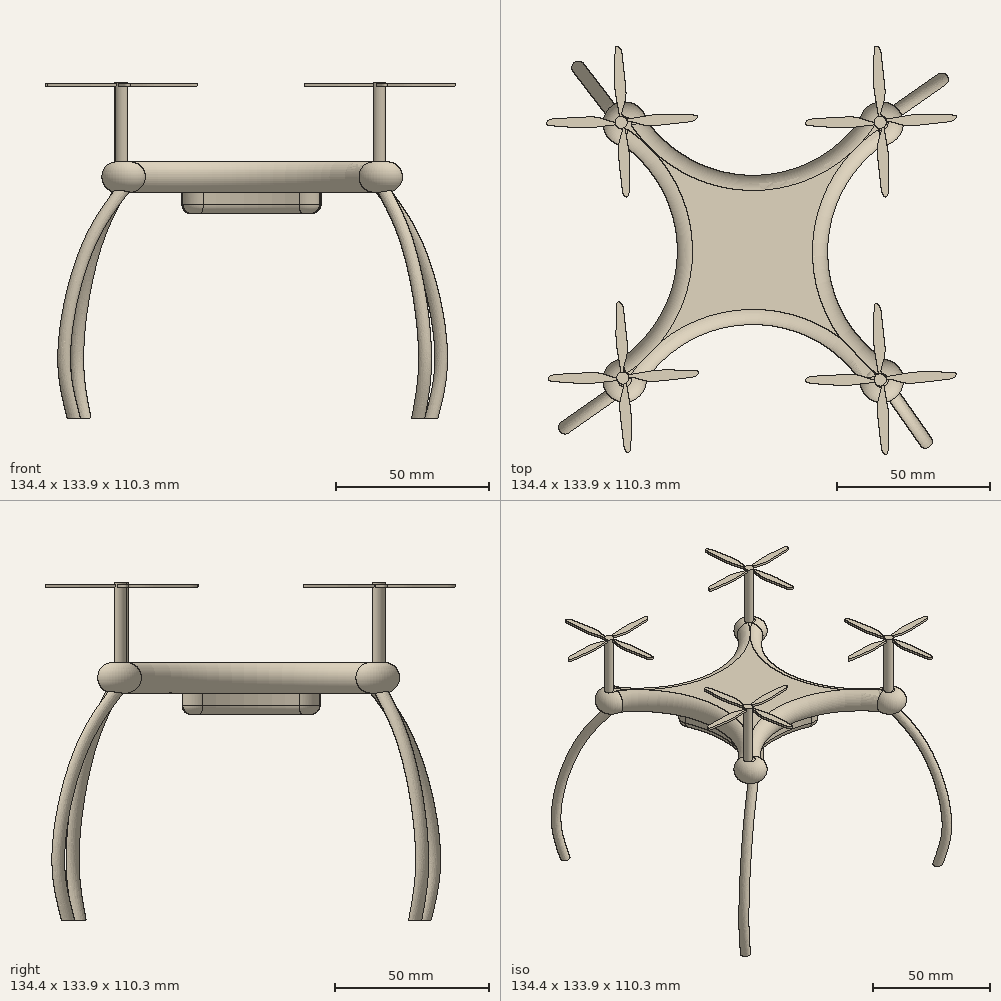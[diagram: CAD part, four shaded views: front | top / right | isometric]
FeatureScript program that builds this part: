
annotation { "Feature Type Name" : "Feature", "Feature Type Description" : "" }
export const myFeature = defineFeature(function(context is Context, id is Id, definition is map)
    precondition{}
    {
        {
            var Q0;
            Q0=qCreatedBy(makeId("Top.planeOp"),FACE);
            var sketch = newSketch(context, id + "F0", { "sketchPlane" : qUnion([Q0])});
            skLineSegment(sketch, "E0.bottom", {"start": v(0, 0) * mm, "end": v(-100, 0) * mm, "construction": true});
            skLineSegment(sketch, "E0.top", {"start": v(0, -100) * mm, "end": v(-100, -100) * mm, "construction": true});
            skLineSegment(sketch, "E0.left", {"start": v(0, 0) * mm, "end": v(0, -100) * mm, "construction": true});
            skLineSegment(sketch, "E0.right", {"start": v(-100, 0) * mm, "end": v(-100, -100) * mm, "construction": true});
            skLineSegment(sketch, "E1", {"start": v(-100, -100) * mm, "end": v(0, 0) * mm, "construction": true});
            skLineSegment(sketch, "E2", {"start": v(-100, 0) * mm, "end": v(0, -100) * mm, "construction": true});
            skArc(sketch, "E3", {"start": v(-93.38, -85.34) * mm, "mid": v(-96.6, -97.94) * mm, "end": v(-85, -92.07) * mm});
            skArc(sketch, "E4", {"start": v(-15, -92.07) * mm, "mid": v(-50, -74.05) * mm, "end": v(-85, -92.07) * mm});
            skArc(sketch, "E5", {"start": v(-15, -92.07) * mm, "mid": v(-3.07, -97.77) * mm, "end": v(-7.58, -85.34) * mm});
            skArc(sketch, "E6", {"start": v(-7.58, -15.34) * mm, "mid": v(-25.6, -50.34) * mm, "end": v(-7.58, -85.34) * mm});
            skArc(sketch, "E7", {"start": v(-7.58, -15.34) * mm, "mid": v(-2.64, -3.44) * mm, "end": v(-15, -7.1) * mm});
            skArc(sketch, "E8", {"start": v(-85, -7.1) * mm, "mid": v(-50, -25.12) * mm, "end": v(-15, -7.1) * mm});
            skArc(sketch, "E9", {"start": v(-85, -7.1) * mm, "mid": v(-97.36, -3.44) * mm, "end": v(-92.43, -15.34) * mm});
            skArc(sketch, "E10", {"start": v(-93.38, -85.34) * mm, "mid": v(-74.89, -50.59) * mm, "end": v(-92.43, -15.34) * mm});
            skSolve(sketch);
        }
        {
            var Q0;
            Q0=makeQuery(id+"F0.imprint","IMPRINT",FACE,{"disambiguationData":[TD([[makeQuery(id+"F0.imprint","IMPRINT",EDGE,{"derivedFrom":sQuery(id+"F0.wireOp",EDGE,"E3")}),1.0]])]});
            extrude(context, id + "F1", {"entities" : qUnion([Q0]), "depth" : 10 * mm, "offsetDistance" : 25 * mm});
        }
        {
            var Q0;
            Q0=makeQuery(id+"F1.opExtrude","CAP_FACE",FACE,{"disambiguationData":[OSD([sQuery(id+"F0.wireOp",EDGE,"E3"),sQuery(id+"F0.wireOp",EDGE,"E4"),sQuery(id+"F0.wireOp",EDGE,"E5"),sQuery(id+"F0.wireOp",EDGE,"E6"),sQuery(id+"F0.wireOp",EDGE,"E7"),sQuery(id+"F0.wireOp",EDGE,"E8"),sQuery(id+"F0.wireOp",EDGE,"E9"),sQuery(id+"F0.wireOp",EDGE,"E10")])],"isStart":false});
            var Q1;
            Q1=makeQuery(id+"F1.opExtrude","CAP_FACE",FACE,{"disambiguationData":[OSD([sQuery(id+"F0.wireOp",EDGE,"E3"),sQuery(id+"F0.wireOp",EDGE,"E4"),sQuery(id+"F0.wireOp",EDGE,"E5"),sQuery(id+"F0.wireOp",EDGE,"E6"),sQuery(id+"F0.wireOp",EDGE,"E7"),sQuery(id+"F0.wireOp",EDGE,"E8"),sQuery(id+"F0.wireOp",EDGE,"E9"),sQuery(id+"F0.wireOp",EDGE,"E10")])],"isStart":true});
            fillet(context, id + "F2", {"entities" : qUnion([Q0, Q1]), "radius" : 5 * mm, "tangentPropagation" : true, "allowEdgeOverflow" : false});
        }
        {
            var Q0;
            Q0=qCreatedBy(makeId("Right.planeOp"),FACE);
            var sketch = newSketch(context, id + "F3", { "sketchPlane" : qUnion([Q0])});
            skFitSpline(sketch, "E11", {"points": [v(21, 0.3) * mm, v(17.73, 12.66) * mm, v(17.36, 24.3) * mm, v(19.55, 37.01) * mm, v(23.54, 49.37) * mm, v(33, 66.1) * mm, v(46.08, 79.9) * mm, v(46.8, 80.27) * mm], "startDerivative": vector(-26.02, 82.97) * mm, "endDerivative": vector(13.83, 3.74) * mm});
            skSolve(sketch);
        }
        {
            var Q0;
            Q0=qCreatedBy(makeId("Top.planeOp"),FACE);
            var sketch = newSketch(context, id + "F4", { "sketchPlane" : qUnion([Q0])});
            skCircle(sketch, "E12", {"center": v(0.33, 21.02) * mm, "radius": 2.16 * mm});
            skSolve(sketch);
        }
        {
            var Q0;
            Q0=makeQuery(id+"F4.imprint","IMPRINT",FACE,{"disambiguationData":[TD([[makeQuery(id+"F4.imprint","IMPRINT",EDGE,{"derivedFrom":sQuery(id+"F4.wireOp",EDGE,"E12")}),1.0]])]});
            var Q1;
            Q1=sQuery(id+"F3.wireOp",EDGE,"E11");
            sweep(context, id + "F5", {"profiles" : qUnion([Q0]), "path" : qUnion([Q1])});
        }
        {
            var Q0;
            Q0=makeQuery(id+"F5.opSweep","SWEPT_BODY",BODY,{"disambiguationData":[OSD([sQuery(id+"F3.wireOp",EDGE,"E11"),sQuery(id+"F4.wireOp",EDGE,"E12")])]});
            transform(context, id + "F6", {"entities" : qUnion([Q0]), "transformType" : TransformType.TRANSLATION_3D, "dx" : -7.8 * mm, "dy" : -134.3 * mm, "dz" : -74.2 * mm, "makeCopy" : false});
        }
        {
            var Q0;
            Q0=makeQuery(id+"F2.opFillet","SPLIT",FACE,{"disambiguationData":[OD(4.0)],"derivedFrom":makeQuery(id+"F1.opExtrude","CAP_FACE",FACE,{"disambiguationData":[OSD([sQuery(id+"F0.wireOp",EDGE,"E3"),sQuery(id+"F0.wireOp",EDGE,"E4"),sQuery(id+"F0.wireOp",EDGE,"E5"),sQuery(id+"F0.wireOp",EDGE,"E6"),sQuery(id+"F0.wireOp",EDGE,"E7"),sQuery(id+"F0.wireOp",EDGE,"E8"),sQuery(id+"F0.wireOp",EDGE,"E9"),sQuery(id+"F0.wireOp",EDGE,"E10")])],"isStart":true})});
            extrude(context, id + "F7", {"entities" : qUnion([Q0]), "operationType" : NewBodyOperationType.ADD, "depth" : 7 * mm, "offsetDistance" : 25 * mm});
        }
        {
            var Q0;
            {var subQ0=sQuery(id+"F0.wireOp",EDGE,"E10");var subQ1=sQuery(id+"F0.wireOp",EDGE,"E9");var subQ2=sQuery(id+"F0.wireOp",EDGE,"E8");var subQ3=sQuery(id+"F0.wireOp",EDGE,"E7");var subQ4=sQuery(id+"F0.wireOp",EDGE,"E6");var subQ5=sQuery(id+"F0.wireOp",EDGE,"E5");var subQ6=sQuery(id+"F0.wireOp",EDGE,"E4");var subQ7=sQuery(id+"F0.wireOp",EDGE,"E3");Q0=makeQuery(id+"F7.opExtrude","SWEPT_EDGE",EDGE,{"disambiguationData":[OSD([subQ7,subQ6,subQ5,subQ4,subQ3,subQ2,subQ1,subQ0]),TDD([makeQuery(id+"F2.opFillet","BLEND_VERTEX",VERTEX,{"disambiguationData":[OD(1.0)],"blendedFrom":[makeQuery(id+"F1.opExtrude","CAP_EDGE",EDGE,{"disambiguationData":[OSD([subQ4])],"isStart":true}),makeQuery(id+"F1.opExtrude","CAP_EDGE",EDGE,{"disambiguationData":[OSD([subQ2])],"isStart":true}),makeQuery(id+"F1.opExtrude","CAP_FACE",FACE,{"disambiguationData":[OSD([subQ7,subQ6,subQ5,subQ4,subQ3,subQ2,subQ1,subQ0])],"isStart":true})],"blendedInto":[makeQuery(id+"F1.opExtrude","CAP_FACE",FACE,{"disambiguationData":[OSD([subQ7,subQ6,subQ5,subQ4,subQ3,subQ2,subQ1,subQ0])],"isStart":true})]})])]});}
            var Q1;
            {var subQ0=sQuery(id+"F0.wireOp",EDGE,"E10");var subQ1=sQuery(id+"F0.wireOp",EDGE,"E9");var subQ2=sQuery(id+"F0.wireOp",EDGE,"E8");var subQ3=sQuery(id+"F0.wireOp",EDGE,"E7");var subQ4=sQuery(id+"F0.wireOp",EDGE,"E6");var subQ5=sQuery(id+"F0.wireOp",EDGE,"E5");var subQ6=sQuery(id+"F0.wireOp",EDGE,"E4");var subQ7=sQuery(id+"F0.wireOp",EDGE,"E3");Q1=makeQuery(id+"F7.opExtrude","SWEPT_EDGE",EDGE,{"disambiguationData":[OSD([subQ7,subQ6,subQ5,subQ4,subQ3,subQ2,subQ1,subQ0]),TDD([makeQuery(id+"F2.opFillet","BLEND_VERTEX",VERTEX,{"disambiguationData":[OD(1.0)],"blendedFrom":[makeQuery(id+"F1.opExtrude","CAP_EDGE",EDGE,{"disambiguationData":[OSD([subQ6])],"isStart":true}),makeQuery(id+"F1.opExtrude","CAP_EDGE",EDGE,{"disambiguationData":[OSD([subQ4])],"isStart":true}),makeQuery(id+"F1.opExtrude","CAP_FACE",FACE,{"disambiguationData":[OSD([subQ7,subQ6,subQ5,subQ4,subQ3,subQ2,subQ1,subQ0])],"isStart":true})],"blendedInto":[makeQuery(id+"F1.opExtrude","CAP_FACE",FACE,{"disambiguationData":[OSD([subQ7,subQ6,subQ5,subQ4,subQ3,subQ2,subQ1,subQ0])],"isStart":true})]})])]});}
            var Q2;
            {var subQ0=sQuery(id+"F0.wireOp",EDGE,"E10");var subQ1=sQuery(id+"F0.wireOp",EDGE,"E9");var subQ2=sQuery(id+"F0.wireOp",EDGE,"E8");var subQ3=sQuery(id+"F0.wireOp",EDGE,"E7");var subQ4=sQuery(id+"F0.wireOp",EDGE,"E6");var subQ5=sQuery(id+"F0.wireOp",EDGE,"E5");var subQ6=sQuery(id+"F0.wireOp",EDGE,"E4");var subQ7=sQuery(id+"F0.wireOp",EDGE,"E3");Q2=makeQuery(id+"F7.opExtrude","SWEPT_EDGE",EDGE,{"disambiguationData":[OSD([subQ7,subQ6,subQ5,subQ4,subQ3,subQ2,subQ1,subQ0]),TDD([makeQuery(id+"F2.opFillet","BLEND_VERTEX",VERTEX,{"disambiguationData":[OD(1.0)],"blendedFrom":[makeQuery(id+"F1.opExtrude","CAP_EDGE",EDGE,{"disambiguationData":[OSD([subQ6])],"isStart":true}),makeQuery(id+"F1.opExtrude","CAP_EDGE",EDGE,{"disambiguationData":[OSD([subQ0])],"isStart":true}),makeQuery(id+"F1.opExtrude","CAP_FACE",FACE,{"disambiguationData":[OSD([subQ7,subQ6,subQ5,subQ4,subQ3,subQ2,subQ1,subQ0])],"isStart":true})],"blendedInto":[makeQuery(id+"F1.opExtrude","CAP_FACE",FACE,{"disambiguationData":[OSD([subQ7,subQ6,subQ5,subQ4,subQ3,subQ2,subQ1,subQ0])],"isStart":true})]})])]});}
            var Q3;
            {var subQ0=sQuery(id+"F0.wireOp",EDGE,"E10");var subQ1=sQuery(id+"F0.wireOp",EDGE,"E9");var subQ2=sQuery(id+"F0.wireOp",EDGE,"E8");var subQ3=sQuery(id+"F0.wireOp",EDGE,"E7");var subQ4=sQuery(id+"F0.wireOp",EDGE,"E6");var subQ5=sQuery(id+"F0.wireOp",EDGE,"E5");var subQ6=sQuery(id+"F0.wireOp",EDGE,"E4");var subQ7=sQuery(id+"F0.wireOp",EDGE,"E3");Q3=makeQuery(id+"F7.opExtrude","SWEPT_EDGE",EDGE,{"disambiguationData":[OSD([subQ7,subQ6,subQ5,subQ4,subQ3,subQ2,subQ1,subQ0]),TDD([makeQuery(id+"F2.opFillet","BLEND_VERTEX",VERTEX,{"blendedFrom":[makeQuery(id+"F1.opExtrude","CAP_EDGE",EDGE,{"disambiguationData":[OSD([subQ2])],"isStart":true}),makeQuery(id+"F1.opExtrude","CAP_EDGE",EDGE,{"disambiguationData":[OSD([subQ0])],"isStart":true}),makeQuery(id+"F1.opExtrude","CAP_FACE",FACE,{"disambiguationData":[OSD([subQ7,subQ6,subQ5,subQ4,subQ3,subQ2,subQ1,subQ0])],"isStart":true})],"blendedInto":[makeQuery(id+"F1.opExtrude","CAP_FACE",FACE,{"disambiguationData":[OSD([subQ7,subQ6,subQ5,subQ4,subQ3,subQ2,subQ1,subQ0])],"isStart":true})]})])]});}
            fillet(context, id + "F8", {"entities" : qUnion([Q0, Q1, Q2, Q3]), "radius" : 5 * mm, "tangentPropagation" : true, "allowEdgeOverflow" : false});
        }
        {
            var Q0;
            {var subQ0=sQuery(id+"F0.wireOp",EDGE,"E10");var subQ1=sQuery(id+"F0.wireOp",EDGE,"E9");var subQ2=sQuery(id+"F0.wireOp",EDGE,"E8");var subQ3=sQuery(id+"F0.wireOp",EDGE,"E7");var subQ4=sQuery(id+"F0.wireOp",EDGE,"E6");var subQ5=sQuery(id+"F0.wireOp",EDGE,"E5");var subQ6=sQuery(id+"F0.wireOp",EDGE,"E4");var subQ7=sQuery(id+"F0.wireOp",EDGE,"E3");Q0=makeQuery(id+"F7.opExtrude","CAP_EDGE",EDGE,{"disambiguationData":[OSD([subQ7,subQ6,subQ5,subQ4,subQ3,subQ2,subQ1,subQ0]),TDD([makeQuery(id+"F2.opFillet","BLEND_EDGE",EDGE,{"disambiguationData":[OD(2.0)],"blendedFrom":[makeQuery(id+"F1.opExtrude","CAP_EDGE",EDGE,{"disambiguationData":[OSD([subQ0])],"isStart":true}),makeQuery(id+"F1.opExtrude","CAP_FACE",FACE,{"disambiguationData":[OSD([subQ7,subQ6,subQ5,subQ4,subQ3,subQ2,subQ1,subQ0])],"isStart":true})],"blendedInto":[makeQuery(id+"F1.opExtrude","CAP_FACE",FACE,{"disambiguationData":[OSD([subQ7,subQ6,subQ5,subQ4,subQ3,subQ2,subQ1,subQ0])],"isStart":true})]})])],"isStart":false});}
            fillet(context, id + "F9", {"entities" : qUnion([Q0]), "radius" : 3 * mm, "tangentPropagation" : true, "allowEdgeOverflow" : false});
        }
        {
            var Q0;
            Q0=qCreatedBy(makeId("Front.planeOp"),FACE);
            var sketch = newSketch(context, id + "F10", { "sketchPlane" : qUnion([Q0])});
            skLineSegment(sketch, "E13", {"start": v(29.76, -0.61) * mm, "end": v(29.76, 29.39) * mm});
            skLineSegment(sketch, "E14", {"start": v(27.76, -0.79) * mm, "end": v(27.76, 29.21) * mm, "construction": true});
            skLineSegment(sketch, "E15", {"start": v(29.76, 29.39) * mm, "end": v(27.76, 29.39) * mm});
            skLineSegment(sketch, "E16", {"start": v(29.76, -0.61) * mm, "end": v(27.76, -0.61) * mm});
            skLineSegment(sketch, "E17", {"start": v(27.76, 29.39) * mm, "end": v(27.76, -0.61) * mm});
            skSolve(sketch);
        }
        {
            var Q0;
            Q0=makeQuery(id+"F10.imprint","IMPRINT",FACE,{"disambiguationData":[TD([[makeQuery(id+"F10.imprint","IMPRINT",EDGE,{"derivedFrom":sQuery(id+"F10.wireOp",EDGE,"E13")}),1.0]])]});
            var Q1;
            Q1=sQuery(id+"F10.wireOp",EDGE,"E17");
            revolve(context, id + "F11", {"entities" : qUnion([Q0]), "axis" : qUnion([Q1]), "revolveType" : RevolveType.FULL});
        }
        {
            var Q0;
            Q0=makeQuery(id+"F11.opRevolve","SWEPT_BODY",BODY,{"disambiguationData":[OSD([sQuery(id+"F10.wireOp",EDGE,"E13"),sQuery(id+"F10.wireOp",EDGE,"E15"),sQuery(id+"F10.wireOp",EDGE,"E16"),sQuery(id+"F10.wireOp",EDGE,"E17")])]});
            transform(context, id + "F12", {"entities" : qUnion([Q0]), "transformType" : TransformType.TRANSLATION_3D, "dx" : -36.1 * mm, "dy" : -92.2 * mm, "dz" : 6.7 * mm, "makeCopy" : false});
        }
        {
            var Q0;
            Q0=qCreatedBy(makeId("Top.planeOp"),FACE);
            var sketch = newSketch(context, id + "F13", { "sketchPlane" : qUnion([Q0])});
            skFitSpline(sketch, "E18", {"points": [v(3.6, 32.66) * mm, v(17.75, 35.15) * mm, v(28.57, 35.98) * mm, v(45.21, 35.57) * mm, v(49.58, 34.53) * mm, v(48.13, 32.03) * mm, v(34.6, 29.95) * mm, v(16.5, 28.5) * mm, v(6.31, 31) * mm, v(4.1, 30.8) * mm], "startDerivative": vector(109.23, 20.77) * mm, "endDerivative": vector(-34.38, -9.02) * mm});
            skLineSegment(sketch, "E19", {"start": v(4.1, 30.8) * mm, "end": v(3.6, 32.66) * mm});
            skCircle(sketch, "E20", {"center": v(0.2, 31) * mm, "radius": 3.9 * mm});
            skFitSpline(sketch, "E21", {"points": [v(2.04, 27.57) * mm, v(4.54, 13.43) * mm, v(5.37, 2.6) * mm, v(4.96, -14.03) * mm, v(3.92, -18.4) * mm, v(1.42, -16.95) * mm, v(-0.66, -3.42) * mm, v(-2.12, 14.68) * mm, v(0.38, 24.87) * mm, v(0.2, 27.08) * mm], "startDerivative": vector(20.77, -109.23) * mm, "endDerivative": vector(-9.02, 34.38) * mm});
            skLineSegment(sketch, "E22", {"start": v(0.2, 27.08) * mm, "end": v(2.04, 27.57) * mm});
            skFitSpline(sketch, "E23", {"points": [v(-3.22, 29.06) * mm, v(-17.48, 27.29) * mm, v(-28.32, 27) * mm, v(-44.92, 28.27) * mm, v(-49.23, 29.54) * mm, v(-47.65, 31.96) * mm, v(-34.04, 33.34) * mm, v(-15.89, 33.87) * mm, v(-5.83, 30.86) * mm, v(-3.62, 30.93) * mm], "startDerivative": vector(-110.15, -15.16) * mm, "endDerivative": vector(34.8, 7.25) * mm});
            skLineSegment(sketch, "E24", {"start": v(-3.62, 30.93) * mm, "end": v(-3.22, 29.06) * mm});
            skFitSpline(sketch, "E25", {"points": [v(-1.47, 34.4) * mm, v(-3.97, 48.55) * mm, v(-4.8, 59.37) * mm, v(-4.38, 76.01) * mm, v(-3.34, 80.38) * mm, v(-0.85, 78.93) * mm, v(1.23, 65.4) * mm, v(2.69, 47.3) * mm, v(0.2, 37.1) * mm, v(0.38, 34.9) * mm], "startDerivative": vector(-20.77, 109.23) * mm, "endDerivative": vector(9.02, -34.38) * mm});
            skLineSegment(sketch, "E26", {"start": v(0.38, 34.9) * mm, "end": v(-1.47, 34.4) * mm});
            skSolve(sketch);
        }
        {
            var Q0;
            Q0 = qSketchRegion(id + "F13", true);
            extrude(context, id + "F14", {"entities" : qUnion([Q0]), "depth" : 2 * mm, "offsetDistance" : 25 * mm});
        }
        {
            var Q0;
            Q0=makeQuery(id+"F14.opExtrude","SWEPT_BODY",BODY,{"disambiguationData":[OSD([sQuery(id+"F13.wireOp",EDGE,"E18"),sQuery(id+"F13.wireOp",EDGE,"E20"),sQuery(id+"F13.wireOp",EDGE,"E21"),sQuery(id+"F13.wireOp",EDGE,"E23"),sQuery(id+"F13.wireOp",EDGE,"E24"),sQuery(id+"F13.wireOp",EDGE,"E25")])]});
            var Q1;
            Q1=makeQuery(id+"F14.opExtrude","CAP_VERTEX",VERTEX,{"disambiguationData":[OSD([sQuery(id+"F13.wireOp",EDGE,"E20"),sQuery(id+"F13.wireOp",EDGE,"E24")])],"isStart":false});
            transform(context, id + "F15", {"entities" : qUnion([Q0]), "transformType" : TransformType.SCALE_UNIFORMLY, "scale" : 0.5, "scalePoint" : qUnion([Q1]), "makeCopy" : false});
        }
        {
            var Q0;
            Q0=makeQuery(id+"F14.opExtrude","SWEPT_BODY",BODY,{"disambiguationData":[OSD([sQuery(id+"F13.wireOp",EDGE,"E18"),sQuery(id+"F13.wireOp",EDGE,"E20"),sQuery(id+"F13.wireOp",EDGE,"E21"),sQuery(id+"F13.wireOp",EDGE,"E23"),sQuery(id+"F13.wireOp",EDGE,"E24"),sQuery(id+"F13.wireOp",EDGE,"E25")])]});
            transform(context, id + "F16", {"entities" : qUnion([Q0]), "transformType" : TransformType.TRANSLATION_3D, "dx" : -6.6 * mm, "dy" : -122 * mm, "dz" : 33.6 * mm, "makeCopy" : false});
        }
        {
            var Q0;
            Q0=makeQuery(id+"F5.opSweep","SWEPT_BODY",BODY,{"disambiguationData":[OSD([sQuery(id+"F3.wireOp",EDGE,"E11"),sQuery(id+"F4.wireOp",EDGE,"E12")])]});
            transform(context, id + "F17", {"entities" : qUnion([Q0]), "transformType" : TransformType.COPY});
        }
        {
            var Q0;
            Q0=makeQuery(id+"F5.opSweep","SWEPT_BODY",BODY,{"disambiguationData":[OSD([sQuery(id+"F3.wireOp",EDGE,"E11"),sQuery(id+"F4.wireOp",EDGE,"E12")])]});
            transform(context, id + "F18", {"entities" : qUnion([Q0]), "transformType" : TransformType.TRANSLATION_3D, "dx" : -83.2 * mm, "dy" : 0 * mm, "dz" : 0 * mm, "makeCopy" : false});
        }
        {
            var Q0;
            Q0=makeQuery(id+"F17.opPattern","COPY",BODY,{"derivedFrom":makeQuery(id+"F5.opSweep","SWEPT_BODY",BODY,{"disambiguationData":[OSD([sQuery(id+"F3.wireOp",EDGE,"E11"),sQuery(id+"F4.wireOp",EDGE,"E12")])]}),"instanceName":"1"});
            var Q1;
            Q1=makeQuery(id+"F14.opExtrude","SWEPT_BODY",BODY,{"disambiguationData":[OSD([sQuery(id+"F13.wireOp",EDGE,"E18"),sQuery(id+"F13.wireOp",EDGE,"E20"),sQuery(id+"F13.wireOp",EDGE,"E21"),sQuery(id+"F13.wireOp",EDGE,"E23"),sQuery(id+"F13.wireOp",EDGE,"E24"),sQuery(id+"F13.wireOp",EDGE,"E25")])]});
            var Q2;
            Q2=makeQuery(id+"F11.opRevolve","SWEPT_BODY",BODY,{"disambiguationData":[OSD([sQuery(id+"F10.wireOp",EDGE,"E13"),sQuery(id+"F10.wireOp",EDGE,"E15"),sQuery(id+"F10.wireOp",EDGE,"E16"),sQuery(id+"F10.wireOp",EDGE,"E17")])]});
            transform(context, id + "F19", {"entities" : qUnion([Q0, Q1, Q2]), "transformType" : TransformType.COPY});
        }
        {
            var Q0;
            Q0=makeQuery(id+"F19.opPattern","COPY",BODY,{"derivedFrom":makeQuery(id+"F17.opPattern","COPY",BODY,{"derivedFrom":makeQuery(id+"F5.opSweep","SWEPT_BODY",BODY,{"disambiguationData":[OSD([sQuery(id+"F3.wireOp",EDGE,"E11"),sQuery(id+"F4.wireOp",EDGE,"E12")])]}),"instanceName":"1"}),"instanceName":"1"});
            var Q1;
            Q1=makeQuery(id+"F11.opRevolve","SWEPT_BODY",BODY,{"disambiguationData":[OSD([sQuery(id+"F10.wireOp",EDGE,"E13"),sQuery(id+"F10.wireOp",EDGE,"E15"),sQuery(id+"F10.wireOp",EDGE,"E16"),sQuery(id+"F10.wireOp",EDGE,"E17")])]});
            var Q2;
            Q2=makeQuery(id+"F14.opExtrude","SWEPT_BODY",BODY,{"disambiguationData":[OSD([sQuery(id+"F13.wireOp",EDGE,"E18"),sQuery(id+"F13.wireOp",EDGE,"E20"),sQuery(id+"F13.wireOp",EDGE,"E21"),sQuery(id+"F13.wireOp",EDGE,"E23"),sQuery(id+"F13.wireOp",EDGE,"E24"),sQuery(id+"F13.wireOp",EDGE,"E25")])]});
            transform(context, id + "F20", {"entities" : qUnion([Q0, Q1, Q2]), "transformType" : TransformType.TRANSLATION_3D, "dx" : 0 * mm, "dy" : 84.4 * mm, "dz" : 0 * mm, "makeCopy" : false});
        }
        {
            var Q0;
            Q0=makeQuery(id+"F19.opPattern","COPY",BODY,{"derivedFrom":makeQuery(id+"F17.opPattern","COPY",BODY,{"derivedFrom":makeQuery(id+"F5.opSweep","SWEPT_BODY",BODY,{"disambiguationData":[OSD([sQuery(id+"F3.wireOp",EDGE,"E11"),sQuery(id+"F4.wireOp",EDGE,"E12")])]}),"instanceName":"1"}),"instanceName":"1"});
            var Q1;
            Q1=makeQuery(id+"F2.opFillet","BLEND_FACE",FACE,{"disambiguationData":[OSD([sQuery(id+"F0.wireOp",EDGE,"E7")])]});
            transform(context, id + "F21", {"entities" : qUnion([Q0]), "transformType" : TransformType.ROTATION, "transformAxis" : qUnion([Q1]), "angle" : 125 * degree, "makeCopy" : false});
        }
        {
            var Q0;
            Q0=makeQuery(id+"F17.opPattern","COPY",BODY,{"derivedFrom":makeQuery(id+"F5.opSweep","SWEPT_BODY",BODY,{"disambiguationData":[OSD([sQuery(id+"F3.wireOp",EDGE,"E11"),sQuery(id+"F4.wireOp",EDGE,"E12")])]}),"instanceName":"1"});
            var Q1;
            Q1=makeQuery(id+"F2.opFillet","BLEND_FACE",FACE,{"disambiguationData":[OSD([sQuery(id+"F0.wireOp",EDGE,"E5")])]});
            transform(context, id + "F22", {"entities" : qUnion([Q0]), "transformType" : TransformType.ROTATION, "transformAxis" : qUnion([Q1]), "angle" : 35 * degree, "makeCopy" : false});
        }
        {
            var Q0;
            Q0=makeQuery(id+"F5.opSweep","SWEPT_BODY",BODY,{"disambiguationData":[OSD([sQuery(id+"F3.wireOp",EDGE,"E11"),sQuery(id+"F4.wireOp",EDGE,"E12")])]});
            var Q1;
            Q1=makeQuery(id+"F2.opFillet","BLEND_FACE",FACE,{"disambiguationData":[OSD([sQuery(id+"F0.wireOp",EDGE,"E3")])]});
            transform(context, id + "F23", {"entities" : qUnion([Q0]), "transformType" : TransformType.ROTATION, "transformAxis" : qUnion([Q1]), "angle" : 55 * degree, "oppositeDirection" : true, "makeCopy" : false});
        }
        {
            var Q0;
            Q0=makeQuery(id+"F19.opPattern","COPY",BODY,{"derivedFrom":makeQuery(id+"F17.opPattern","COPY",BODY,{"derivedFrom":makeQuery(id+"F5.opSweep","SWEPT_BODY",BODY,{"disambiguationData":[OSD([sQuery(id+"F3.wireOp",EDGE,"E11"),sQuery(id+"F4.wireOp",EDGE,"E12")])]}),"instanceName":"1"}),"instanceName":"1"});
            var Q1;
            Q1=makeQuery(id+"F11.opRevolve","SWEPT_BODY",BODY,{"disambiguationData":[OSD([sQuery(id+"F10.wireOp",EDGE,"E13"),sQuery(id+"F10.wireOp",EDGE,"E15"),sQuery(id+"F10.wireOp",EDGE,"E16"),sQuery(id+"F10.wireOp",EDGE,"E17")])]});
            var Q2;
            Q2=makeQuery(id+"F14.opExtrude","SWEPT_BODY",BODY,{"disambiguationData":[OSD([sQuery(id+"F13.wireOp",EDGE,"E18"),sQuery(id+"F13.wireOp",EDGE,"E20"),sQuery(id+"F13.wireOp",EDGE,"E21"),sQuery(id+"F13.wireOp",EDGE,"E23"),sQuery(id+"F13.wireOp",EDGE,"E24"),sQuery(id+"F13.wireOp",EDGE,"E25")])]});
            transform(context, id + "F24", {"entities" : qUnion([Q0, Q1, Q2]), "transformType" : TransformType.COPY});
        }
        {
            var Q0;
            Q0=makeQuery(id+"F14.opExtrude","SWEPT_BODY",BODY,{"disambiguationData":[OSD([sQuery(id+"F13.wireOp",EDGE,"E18"),sQuery(id+"F13.wireOp",EDGE,"E20"),sQuery(id+"F13.wireOp",EDGE,"E21"),sQuery(id+"F13.wireOp",EDGE,"E23"),sQuery(id+"F13.wireOp",EDGE,"E24"),sQuery(id+"F13.wireOp",EDGE,"E25")])]});
            var Q1;
            Q1=makeQuery(id+"F11.opRevolve","SWEPT_BODY",BODY,{"disambiguationData":[OSD([sQuery(id+"F10.wireOp",EDGE,"E13"),sQuery(id+"F10.wireOp",EDGE,"E15"),sQuery(id+"F10.wireOp",EDGE,"E16"),sQuery(id+"F10.wireOp",EDGE,"E17")])]});
            var Q2;
            Q2=makeQuery(id+"F19.opPattern","COPY",BODY,{"derivedFrom":makeQuery(id+"F17.opPattern","COPY",BODY,{"derivedFrom":makeQuery(id+"F5.opSweep","SWEPT_BODY",BODY,{"disambiguationData":[OSD([sQuery(id+"F3.wireOp",EDGE,"E11"),sQuery(id+"F4.wireOp",EDGE,"E12")])]}),"instanceName":"1"}),"instanceName":"1"});
            transform(context, id + "F25", {"entities" : qUnion([Q0, Q1, Q2]), "transformType" : TransformType.TRANSLATION_3D, "dx" : -84.9 * mm, "dy" : 0 * mm, "dz" : 0 * mm, "makeCopy" : false});
        }
        {
            var Q0;
            Q0=makeQuery(id+"F19.opPattern","COPY",BODY,{"derivedFrom":makeQuery(id+"F17.opPattern","COPY",BODY,{"derivedFrom":makeQuery(id+"F5.opSweep","SWEPT_BODY",BODY,{"disambiguationData":[OSD([sQuery(id+"F3.wireOp",EDGE,"E11"),sQuery(id+"F4.wireOp",EDGE,"E12")])]}),"instanceName":"1"}),"instanceName":"1"});
            var Q1;
            Q1=makeQuery(id+"F2.opFillet","BLEND_FACE",FACE,{"disambiguationData":[OSD([sQuery(id+"F0.wireOp",EDGE,"E9")])]});
            transform(context, id + "F26", {"entities" : qUnion([Q0]), "transformType" : TransformType.ROTATION, "transformAxis" : qUnion([Q1]), "angle" : 92.47 * degree, "makeCopy" : false});
        }
        {
            var Q0;
            Q0=makeQuery(id+"F14.opExtrude","SWEPT_BODY",BODY,{"disambiguationData":[OSD([sQuery(id+"F13.wireOp",EDGE,"E18"),sQuery(id+"F13.wireOp",EDGE,"E20"),sQuery(id+"F13.wireOp",EDGE,"E21"),sQuery(id+"F13.wireOp",EDGE,"E23"),sQuery(id+"F13.wireOp",EDGE,"E24"),sQuery(id+"F13.wireOp",EDGE,"E25")])]});
            var Q1;
            Q1=makeQuery(id+"F11.opRevolve","SWEPT_BODY",BODY,{"disambiguationData":[OSD([sQuery(id+"F10.wireOp",EDGE,"E13"),sQuery(id+"F10.wireOp",EDGE,"E15"),sQuery(id+"F10.wireOp",EDGE,"E16"),sQuery(id+"F10.wireOp",EDGE,"E17")])]});
            transform(context, id + "F27", {"entities" : qUnion([Q0, Q1]), "transformType" : TransformType.COPY});
        }
        {
            var Q0;
            Q0=makeQuery(id+"F11.opRevolve","SWEPT_BODY",BODY,{"disambiguationData":[OSD([sQuery(id+"F10.wireOp",EDGE,"E13"),sQuery(id+"F10.wireOp",EDGE,"E15"),sQuery(id+"F10.wireOp",EDGE,"E16"),sQuery(id+"F10.wireOp",EDGE,"E17")])]});
            var Q1;
            Q1=makeQuery(id+"F14.opExtrude","SWEPT_BODY",BODY,{"disambiguationData":[OSD([sQuery(id+"F13.wireOp",EDGE,"E18"),sQuery(id+"F13.wireOp",EDGE,"E20"),sQuery(id+"F13.wireOp",EDGE,"E21"),sQuery(id+"F13.wireOp",EDGE,"E23"),sQuery(id+"F13.wireOp",EDGE,"E24"),sQuery(id+"F13.wireOp",EDGE,"E25")])]});
            transform(context, id + "F28", {"entities" : qUnion([Q0, Q1]), "transformType" : TransformType.TRANSLATION_3D, "dx" : 0.5 * mm, "dy" : -83.8 * mm, "dz" : 0 * mm, "makeCopy" : false});
        }
    });
